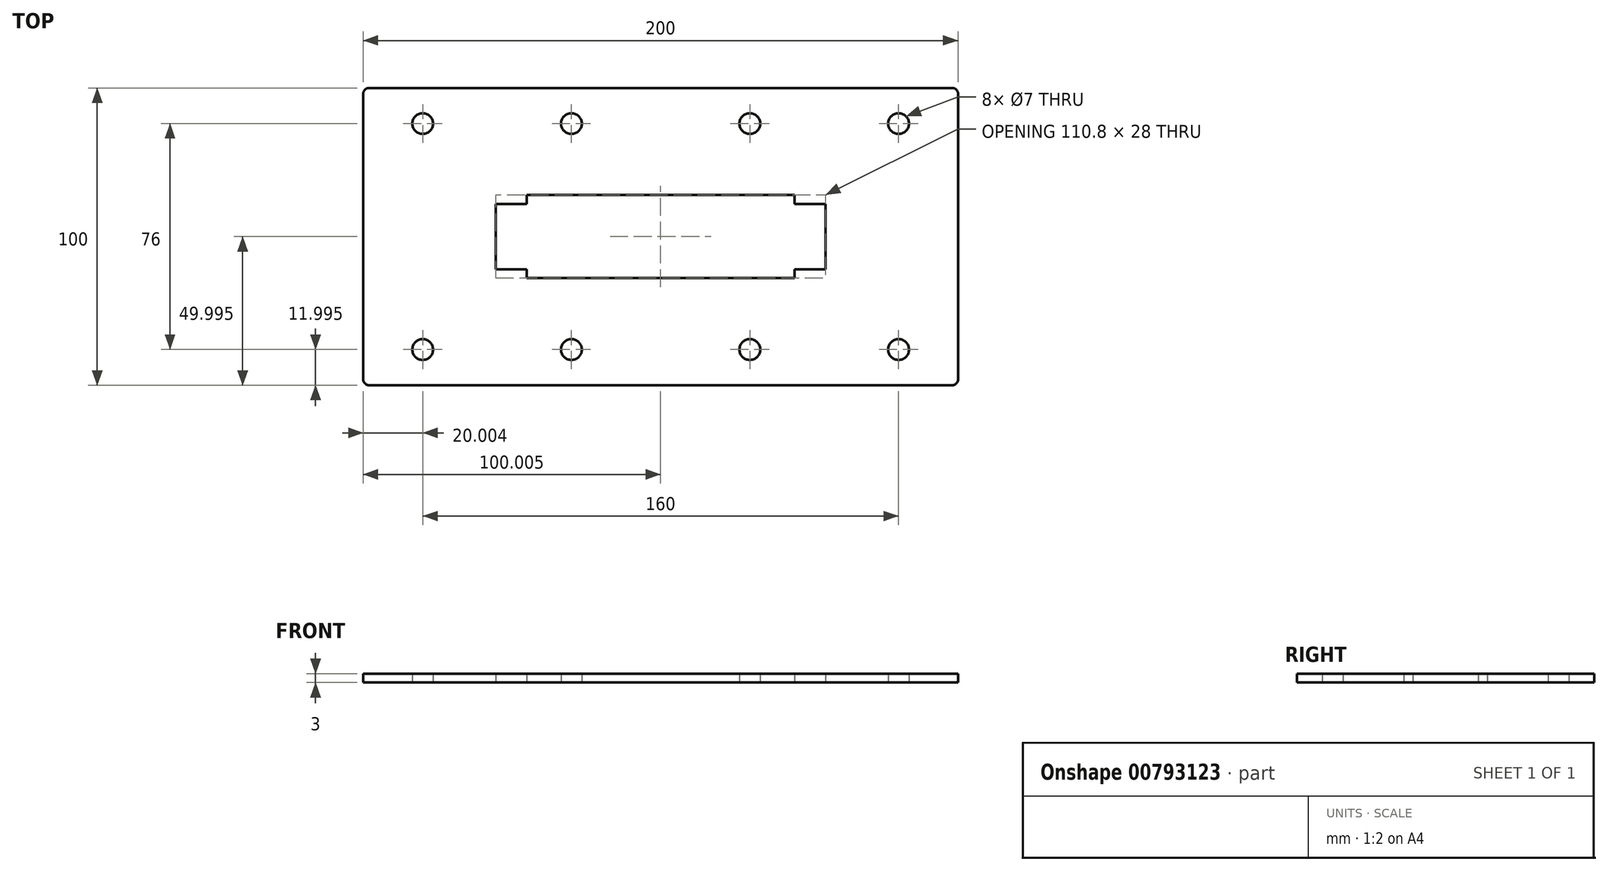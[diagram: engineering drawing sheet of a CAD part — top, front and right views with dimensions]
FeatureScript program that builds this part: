
annotation { "Feature Type Name" : "Feature", "Feature Type Description" : "" }
export const myFeature = defineFeature(function(context is Context, id is Id, definition is map)
    precondition{}
    {
        {
            var Q0;
            Q0=qCreatedBy(makeId("Top.planeOp"),FACE);
            var sketch = newSketch(context, id + "F0", { "sketchPlane" : qUnion([Q0])});
            skLineSegment(sketch, "E0", {"start": v(-145.97, 27.7) * mm, "end": v(-125.97, 27.7) * mm});
            skLineSegment(sketch, "E1", {"start": v(-125.97, 27.7) * mm, "end": v(-75.97, 27.7) * mm});
            skLineSegment(sketch, "E2", {"start": v(-75.97, 27.7) * mm, "end": v(-15.97, 27.7) * mm});
            skLineSegment(sketch, "E3", {"start": v(-15.97, 27.7) * mm, "end": v(34.03, 27.7) * mm});
            skLineSegment(sketch, "E4", {"start": v(34.03, 27.7) * mm, "end": v(52.03, 27.7) * mm});
            skLineSegment(sketch, "E5", {"start": v(54.03, 25.7) * mm, "end": v(54.03, -70.3) * mm});
            skLineSegment(sketch, "E6", {"start": v(52.03, -72.3) * mm, "end": v(-145.97, -72.3) * mm});
            skLineSegment(sketch, "E7", {"start": v(-145.97, -70.3) * mm, "end": v(-145.97, 25.7) * mm});
            skLineSegment(sketch, "E8", {"start": v(-90.97, -8.3) * mm, "end": v(-0.97, -8.3) * mm});
            skLineSegment(sketch, "E9", {"start": v(-0.97, -8.3) * mm, "end": v(-0.97, -11.3) * mm});
            skLineSegment(sketch, "E10", {"start": v(-0.97, -11.3) * mm, "end": v(9.43, -11.3) * mm});
            skLineSegment(sketch, "E11", {"start": v(9.43, -11.3) * mm, "end": v(9.43, -33.3) * mm});
            skLineSegment(sketch, "E12", {"start": v(9.43, -33.3) * mm, "end": v(-0.97, -33.3) * mm});
            skLineSegment(sketch, "E13", {"start": v(-0.97, -33.3) * mm, "end": v(-0.97, -36.3) * mm});
            skLineSegment(sketch, "E14", {"start": v(-0.97, -36.3) * mm, "end": v(-90.97, -36.3) * mm});
            skLineSegment(sketch, "E15", {"start": v(-90.97, -36.3) * mm, "end": v(-90.97, -33.3) * mm});
            skLineSegment(sketch, "E16", {"start": v(-90.97, -33.3) * mm, "end": v(-101.37, -33.3) * mm});
            skLineSegment(sketch, "E17", {"start": v(-101.37, -33.3) * mm, "end": v(-101.37, -11.3) * mm});
            skLineSegment(sketch, "E18", {"start": v(-101.37, -11.3) * mm, "end": v(-90.97, -11.3) * mm});
            skLineSegment(sketch, "E19", {"start": v(-90.97, -11.3) * mm, "end": v(-90.97, -8.3) * mm});
            skLineSegment(sketch, "E20", {"start": v(-143.97, 27.7) * mm, "end": v(-45.97, 27.7) * mm, "construction": true});
            skLineSegment(sketch, "E21", {"start": v(-45.97, 27.7) * mm, "end": v(-45.97, -36.3) * mm, "construction": true});
            skLineSegment(sketch, "E22", {"start": v(-90.97, -36.3) * mm, "end": v(-45.97, -36.3) * mm, "construction": true});
            skLineSegment(sketch, "E23", {"start": v(-143.97, -72.3) * mm, "end": v(-125.97, -72.3) * mm, "construction": true});
            skLineSegment(sketch, "E24", {"start": v(-125.97, -72.3) * mm, "end": v(-125.97, -60.3) * mm, "construction": true});
            skLineSegment(sketch, "E25", {"start": v(-125.97, -60.3) * mm, "end": v(-75.97, -60.3) * mm, "construction": true});
            skLineSegment(sketch, "E26", {"start": v(-75.97, -60.3) * mm, "end": v(-15.97, -60.3) * mm, "construction": true});
            skLineSegment(sketch, "E27", {"start": v(-15.97, -60.3) * mm, "end": v(34.03, -60.3) * mm, "construction": true});
            skLineSegment(sketch, "E28", {"start": v(34.03, -60.3) * mm, "end": v(34.03, -72.3) * mm, "construction": true});
            skCircle(sketch, "E29", {"center": v(-125.97, -60.3) * mm, "radius": 3.5 * mm});
            skCircle(sketch, "E30", {"center": v(-75.97, -60.3) * mm, "radius": 3.5 * mm});
            skCircle(sketch, "E31", {"center": v(-15.97, -60.3) * mm, "radius": 3.5 * mm});
            skCircle(sketch, "E32", {"center": v(34.03, -60.3) * mm, "radius": 3.5 * mm});
            skLineSegment(sketch, "E33", {"start": v(-145.97, -22.3) * mm, "end": v(54.03, -22.3) * mm, "construction": true});
            skCircle(sketch, "E34.MirrorC", {"center": v(34.03, 15.7) * mm, "radius": 3.5 * mm});
            skCircle(sketch, "E35.MirrorC", {"center": v(-125.97, 15.7) * mm, "radius": 3.5 * mm});
            skCircle(sketch, "E36.MirrorC", {"center": v(-15.97, 15.7) * mm, "radius": 3.5 * mm});
            skLineSegment(sketch, "E37.MirrorCS", {"start": v(-75.97, 15.7) * mm, "end": v(-15.97, 15.7) * mm, "construction": true});
            skLineSegment(sketch, "E38.MirrorCS", {"start": v(-125.97, 15.7) * mm, "end": v(-75.97, 15.7) * mm, "construction": true});
            skLineSegment(sketch, "E39.MirrorCS", {"start": v(-15.97, 15.7) * mm, "end": v(34.03, 15.7) * mm, "construction": true});
            skCircle(sketch, "E40.MirrorC", {"center": v(-75.97, 15.7) * mm, "radius": 3.5 * mm});
            skPoint(sketch, "E41.visualSharp", {"position": v(-145.97, 27.7) * mm});
            skArc(sketch, "E41.filletArc", {"start": v(-143.97, 27.7) * mm, "mid": v(-145.38, 27.12) * mm, "end": v(-145.97, 25.7) * mm});
            skPoint(sketch, "E42.visualSharp", {"position": v(-145.97, -72.3) * mm});
            skArc(sketch, "E42.filletArc", {"start": v(-145.97, -70.3) * mm, "mid": v(-145.38, -71.7) * mm, "end": v(-143.97, -72.3) * mm});
            skPoint(sketch, "E43.visualSharp", {"position": v(54.03, -72.3) * mm});
            skArc(sketch, "E43.filletArc", {"start": v(52.03, -72.3) * mm, "mid": v(53.45, -71.7) * mm, "end": v(54.03, -70.3) * mm});
            skPoint(sketch, "E44.visualSharp", {"position": v(54.03, 27.7) * mm});
            skArc(sketch, "E44.filletArc", {"start": v(54.03, 25.7) * mm, "mid": v(53.45, 27.12) * mm, "end": v(52.03, 27.7) * mm});
            skSolve(sketch);
        }
        {
            var Q0;
            Q0 = qSketchRegion(id + "F0", true);
            extrude(context, id + "F1", {"entities" : qUnion([Q0]), "depth" : 3 * mm, "offsetDistance" : 25 * mm});
        }
    });
